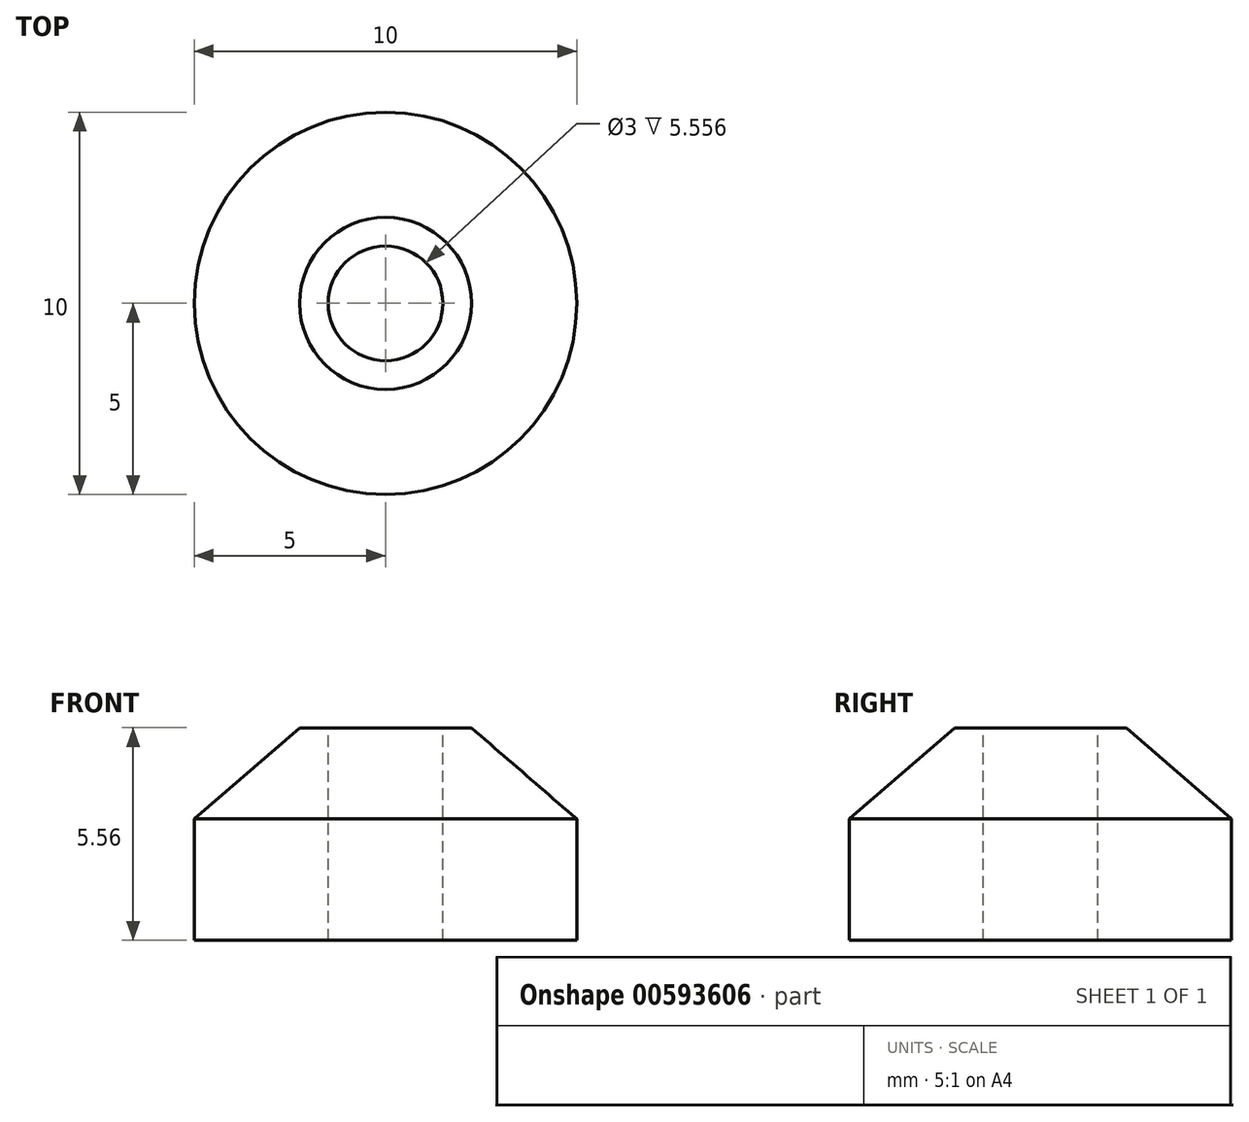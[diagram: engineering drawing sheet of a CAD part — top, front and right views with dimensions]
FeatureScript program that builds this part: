
annotation { "Feature Type Name" : "Feature", "Feature Type Description" : "" }
export const myFeature = defineFeature(function(context is Context, id is Id, definition is map)
    precondition{}
    {
        {
            var Q0;
            Q0=qCreatedBy(makeId("Top.planeOp"),FACE);
            var sketch = newSketch(context, id + "F0", { "sketchPlane" : qUnion([Q0])});
            skCircle(sketch, "E0", {"center": v(0, 0) * mm, "radius": 5 * mm});
            skSolve(sketch);
        }
        {
            var Q0;
            Q0=qCreatedBy(makeId("Top.planeOp"),FACE);
            cPlane(context, id + "F1", {"entities" : qUnion([Q0]), "cplaneType" : CPlaneType.OFFSET, "offset" : 5.56 * mm, "width" : 152.4 * mm, "height" : 152.4 * mm});
        }
        {
            var Q0;
            Q0=makeQuery(id+"F0.imprint","IMPRINT",FACE,{"disambiguationData":[TD([[makeQuery(id+"F0.imprint","IMPRINT",EDGE,{"derivedFrom":sQuery(id+"F0.wireOp",EDGE,"E0")}),1.0]])]});
            extrude(context, id + "F2", {"entities" : qUnion([Q0]), "depth" : 3.17 * mm, "offsetDistance" : 25.4 * mm});
        }
        {
            var Q0;
            Q0=qCreatedBy(id+"F1.planeOp",FACE);
            var sketch = newSketch(context, id + "F3", { "sketchPlane" : qUnion([Q0])});
            skCircle(sketch, "E1", {"center": v(0, 0) * mm, "radius": 2.25 * mm});
            skSolve(sketch);
        }
        {
            var Q1;
            Q1=makeQuery(id+"F2.opExtrude","CAP_FACE",FACE,{"disambiguationData":[OSD([sQuery(id+"F0.wireOp",EDGE,"E0")])],"isStart":false});
            var Q2;
            Q2=makeQuery(id+"F3.imprint","IMPRINT",FACE,{"disambiguationData":[TD([[makeQuery(id+"F3.imprint","IMPRINT",EDGE,{"derivedFrom":sQuery(id+"F3.wireOp",EDGE,"E1")}),1.0]])]});
            loft(context, id + "F4", {"operationType" : NewBodyOperationType.ADD, "sheetProfilesArray" : [{ "sheetProfileEntities" : qUnion([Q1]) }, { "sheetProfileEntities" : qUnion([Q2]) }]});
        }
        {
            var Q0;
            Q0=makeQuery(id+"F4.opLoft","CAP_FACE",FACE,{"disambiguationData":[OSD([makeQuery(id+"F3.imprint","IMPRINT",FACE,{"disambiguationData":[TD([[makeQuery(id+"F3.imprint","IMPRINT",EDGE,{"derivedFrom":sQuery(id+"F3.wireOp",EDGE,"E1")}),1.0]])]})])],"isStart":true});
            var sketch = newSketch(context, id + "F5", { "sketchPlane" : qUnion([Q0])});
            skCircle(sketch, "E2", {"center": v(0, 0) * mm, "radius": 1.5 * mm});
            skSolve(sketch);
        }
        {
            var Q0;
            Q0 = qSketchRegion(id + "F5", true);
            extrude(context, id + "F6", {"entities" : qUnion([Q0]), "operationType" : NewBodyOperationType.REMOVE, "oppositeDirection" : true, "depth" : 25.4 * mm, "offsetDistance" : 25.4 * mm});
        }
    });
